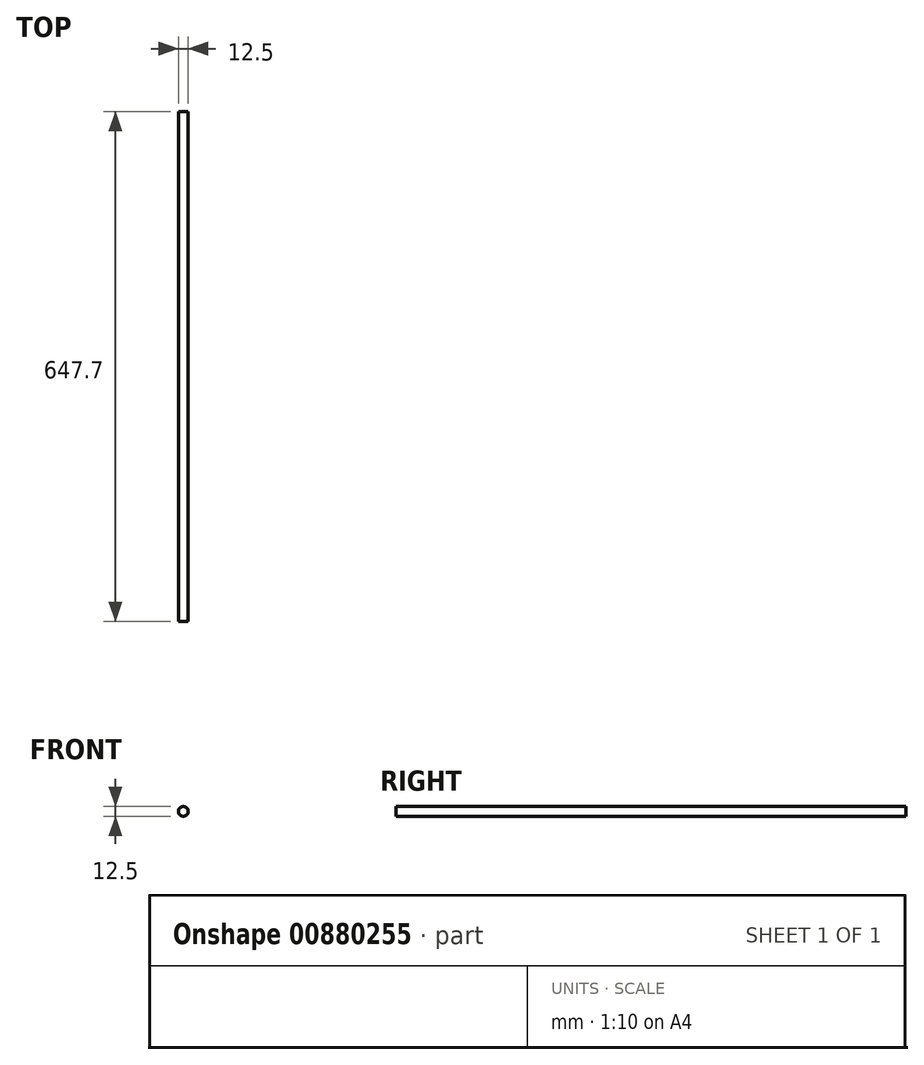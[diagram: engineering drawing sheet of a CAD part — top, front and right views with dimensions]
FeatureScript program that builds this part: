
annotation { "Feature Type Name" : "Feature", "Feature Type Description" : "" }
export const myFeature = defineFeature(function(context is Context, id is Id, definition is map)
    precondition{}
    {
        {
            var Q0;
            Q0=qCreatedBy(makeId("Front.planeOp"),FACE);
            var sketch = newSketch(context, id + "F0", { "sketchPlane" : qUnion([Q0])});
            skCircle(sketch, "E0", {"center": v(0, 0) * mm, "radius": 6.25 * mm});
            skSolve(sketch);
        }
        {
            var Q0;
            Q0=qSketchRegion(id+"F0",true);
            extrude(context, id + "F1", {"entities" : qUnion([Q0]), "depth" : 647.7 * mm});
        }
    });
